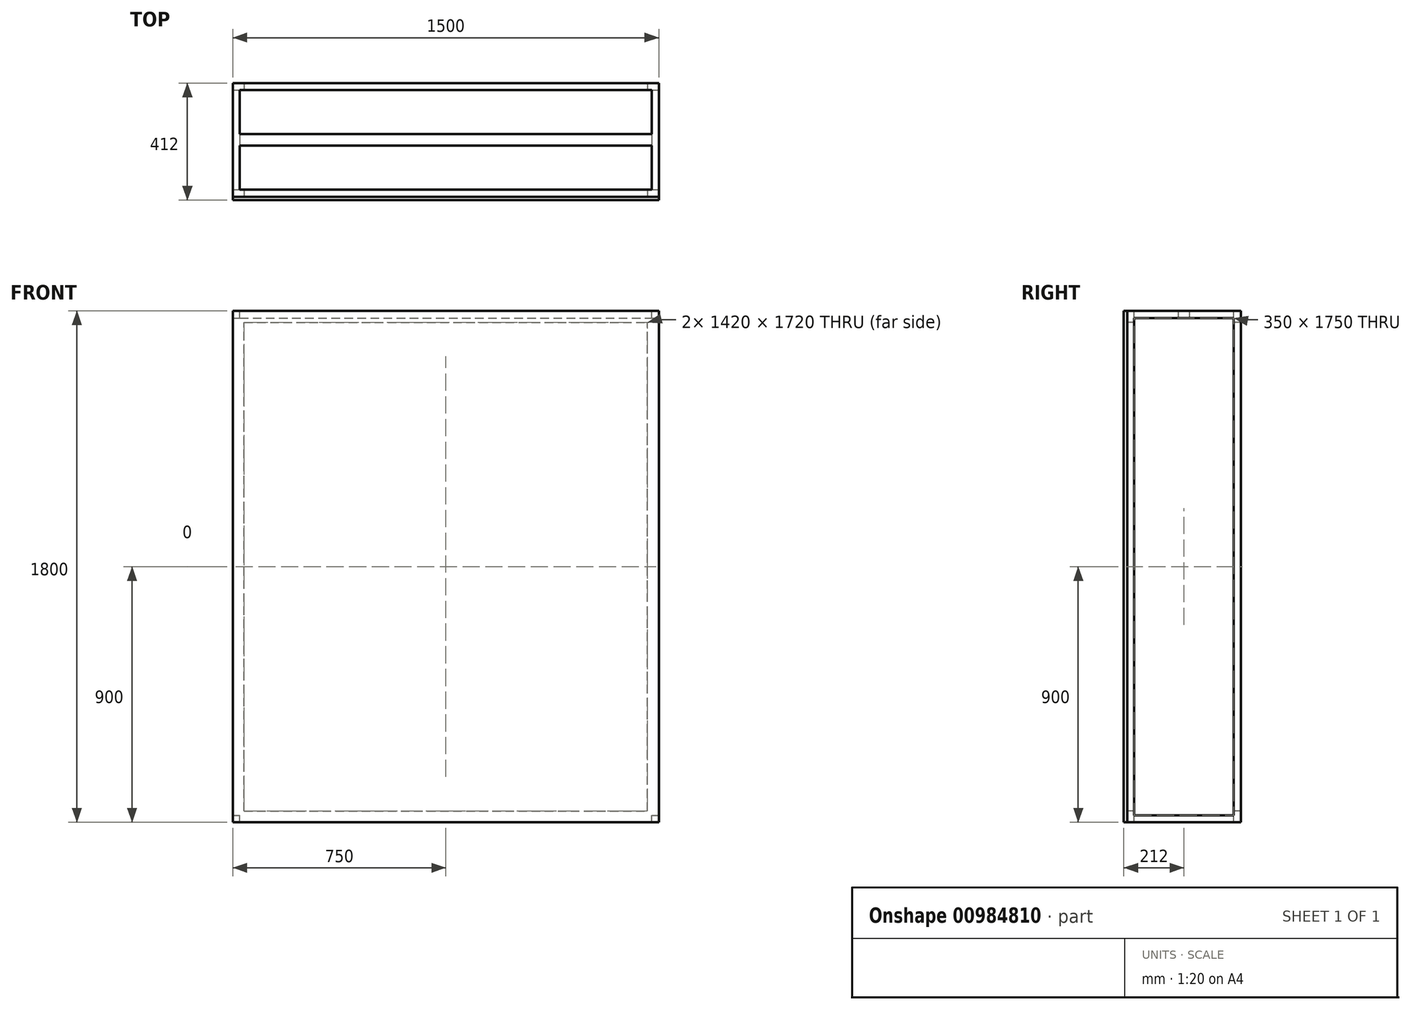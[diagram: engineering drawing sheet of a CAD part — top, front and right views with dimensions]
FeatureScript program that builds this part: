
annotation { "Feature Type Name" : "Feature", "Feature Type Description" : "" }
export const myFeature = defineFeature(function(context is Context, id is Id, definition is map)
    precondition{}
    {
        {
            var Q0;
            Q0=qCreatedBy(makeId("Top.planeOp"),FACE);
            var sketch = newSketch(context, id + "F0", { "sketchPlane" : qUnion([Q0])});
            skLineSegment(sketch, "E0.bottom", {"start": v(750, 200) * mm, "end": v(-750, 200) * mm});
            skLineSegment(sketch, "E0.top", {"start": v(750, -200) * mm, "end": v(-750, -200) * mm});
            skLineSegment(sketch, "E0.left", {"start": v(750, 200) * mm, "end": v(750, -200) * mm});
            skLineSegment(sketch, "E0.right", {"start": v(-750, 200) * mm, "end": v(-750, -200) * mm});
            skPoint(sketch, "E0.middle", {"position": v(0, 0) * mm});
            skSolve(sketch);
        }
        {
            var Q0;
            Q0 = qSketchRegion(id + "F0", true);
            extrude(context, id + "F1", {"entities" : qUnion([Q0]), "endBound" : BoundingType.SYMMETRIC, "depth" : 1800 * mm, "offsetDistance" : 25 * mm});
        }
        {
            var Q0;
            Q0=makeQuery(id+"F1.opExtrude","SWEPT_FACE",FACE,{"disambiguationData":[OSD([sQuery(id+"F0.wireOp",EDGE,"E0.top")])]});
            var sketch = newSketch(context, id + "F2", { "sketchPlane" : qUnion([Q0])});
            skLineSegment(sketch, "E1.bottom", {"start": v(710, 860) * mm, "end": v(-710, 860) * mm});
            skLineSegment(sketch, "E1.top", {"start": v(710, -860) * mm, "end": v(-710, -860) * mm});
            skLineSegment(sketch, "E1.left", {"start": v(710, 860) * mm, "end": v(710, -860) * mm});
            skLineSegment(sketch, "E1.right", {"start": v(-710, 860) * mm, "end": v(-710, -860) * mm});
            skPoint(sketch, "E1.middle", {"position": v(0, 0) * mm});
            skSolve(sketch);
        }
        {
            var Q0;
            Q0 = qSketchRegion(id + "F2", true);
            extrude(context, id + "F3", {"entities" : qUnion([Q0]), "operationType" : NewBodyOperationType.REMOVE, "endBound" : BoundingType.THROUGH_ALL, "oppositeDirection" : true, "depth" : 25 * mm, "offsetDistance" : 25 * mm});
        }
        {
            var Q0;
            Q0=makeQuery(id+"F1.opExtrude","SWEPT_FACE",FACE,{"disambiguationData":[OSD([sQuery(id+"F0.wireOp",EDGE,"E0.left")])]});
            var sketch = newSketch(context, id + "F4", { "sketchPlane" : qUnion([Q0])});
            skLineSegment(sketch, "E2.bottom", {"start": v(175, 875) * mm, "end": v(-175, 875) * mm});
            skLineSegment(sketch, "E2.top", {"start": v(175, -875) * mm, "end": v(-175, -875) * mm});
            skLineSegment(sketch, "E2.left", {"start": v(175, 875) * mm, "end": v(175, -875) * mm});
            skLineSegment(sketch, "E2.right", {"start": v(-175, 875) * mm, "end": v(-175, -875) * mm});
            skPoint(sketch, "E2.middle", {"position": v(0, 0) * mm});
            skSolve(sketch);
        }
        {
            var Q0;
            Q0 = qSketchRegion(id + "F4", true);
            extrude(context, id + "F5", {"entities" : qUnion([Q0]), "operationType" : NewBodyOperationType.REMOVE, "endBound" : BoundingType.THROUGH_ALL, "oppositeDirection" : true, "depth" : 25 * mm, "offsetDistance" : 25 * mm});
        }
        {
            var Q0;
            Q0=makeQuery(id+"F1.opExtrude","CAP_FACE",FACE,{"disambiguationData":[OSD([sQuery(id+"F0.wireOp",EDGE,"E0.bottom"),sQuery(id+"F0.wireOp",EDGE,"E0.top"),sQuery(id+"F0.wireOp",EDGE,"E0.left"),sQuery(id+"F0.wireOp",EDGE,"E0.right")])],"isStart":false});
            var sketch = newSketch(context, id + "F6", { "sketchPlane" : qUnion([Q0])});
            skLineSegment(sketch, "E3.bottom", {"start": v(725, 175) * mm, "end": v(-725, 175) * mm});
            skLineSegment(sketch, "E3.top", {"start": v(725, -175) * mm, "end": v(-725, -175) * mm});
            skLineSegment(sketch, "E3.left", {"start": v(725, 175) * mm, "end": v(725, -175) * mm});
            skLineSegment(sketch, "E3.right", {"start": v(-725, 175) * mm, "end": v(-725, -175) * mm});
            skPoint(sketch, "E3.middle", {"position": v(0, 0) * mm});
            skSolve(sketch);
        }
        {
            var Q0;
            Q0 = qSketchRegion(id + "F6", true);
            extrude(context, id + "F7", {"entities" : qUnion([Q0]), "operationType" : NewBodyOperationType.REMOVE, "endBound" : BoundingType.THROUGH_ALL, "oppositeDirection" : true, "depth" : 25 * mm, "offsetDistance" : 25 * mm});
        }
        {
            var Q0;
            Q0=makeQuery(id+"F1.opExtrude","CAP_FACE",FACE,{"disambiguationData":[OSD([sQuery(id+"F0.wireOp",EDGE,"E0.bottom"),sQuery(id+"F0.wireOp",EDGE,"E0.top"),sQuery(id+"F0.wireOp",EDGE,"E0.left"),sQuery(id+"F0.wireOp",EDGE,"E0.right")])],"isStart":false});
            var sketch = newSketch(context, id + "F8", { "sketchPlane" : qUnion([Q0])});
            skLineSegment(sketch, "E4.bottom", {"start": v(-725, 20) * mm, "end": v(725, 20) * mm});
            skLineSegment(sketch, "E4.top", {"start": v(-725, -20) * mm, "end": v(725, -20) * mm});
            skLineSegment(sketch, "E4.left", {"start": v(-725, 20) * mm, "end": v(-725, -20) * mm});
            skLineSegment(sketch, "E4.right", {"start": v(725, 20) * mm, "end": v(725, -20) * mm});
            skPoint(sketch, "E4.middle", {"position": v(0, 0) * mm});
            skSolve(sketch);
        }
        {
            var Q0;
            Q0 = qSketchRegion(id + "F8", true);
            extrude(context, id + "F9", {"entities" : qUnion([Q0]), "operationType" : NewBodyOperationType.ADD, "oppositeDirection" : true, "depth" : 25 * mm, "offsetDistance" : 25 * mm});
        }
        {
            var Q0;
            Q0=makeQuery(id+"F1.opExtrude","SWEPT_FACE",FACE,{"disambiguationData":[OSD([sQuery(id+"F0.wireOp",EDGE,"E0.right")])]});
            var sketch = newSketch(context, id + "F10", { "sketchPlane" : qUnion([Q0])});
            skLineSegment(sketch, "E5.bottom", {"start": v(-12.5, 875) * mm, "end": v(12.5, 875) * mm});
            skLineSegment(sketch, "E5.top", {"start": v(-12.5, -875) * mm, "end": v(12.5, -875) * mm});
            skLineSegment(sketch, "E5.left", {"start": v(-12.5, 875) * mm, "end": v(-12.5, -875) * mm});
            skLineSegment(sketch, "E5.right", {"start": v(12.5, 875) * mm, "end": v(12.5, -875) * mm});
            skPoint(sketch, "E5.middle", {"position": v(0, 0) * mm});
            skSolve(sketch);
        }
        {
            var Q0;
            Q0=makeQuery(id+"F1.opExtrude","SWEPT_FACE",FACE,{"disambiguationData":[OSD([sQuery(id+"F0.wireOp",EDGE,"E0.top")])]});
            var sketch = newSketch(context, id + "F11", { "sketchPlane" : qUnion([Q0])});
            skLineSegment(sketch, "E6.bottom", {"start": v(-750, 900) * mm, "end": v(750, 900) * mm});
            skLineSegment(sketch, "E6.top", {"start": v(-750, -900) * mm, "end": v(750, -900) * mm});
            skLineSegment(sketch, "E6.left", {"start": v(-750, 900) * mm, "end": v(-750, -900) * mm});
            skLineSegment(sketch, "E6.right", {"start": v(750, 900) * mm, "end": v(750, -900) * mm});
            skSolve(sketch);
        }
        {
            var Q0;
            Q0 = qSketchRegion(id + "F11", true);
            extrude(context, id + "F12", {"entities" : qUnion([Q0]), "depth" : 12 * mm, "offsetDistance" : 25 * mm});
        }
    });
